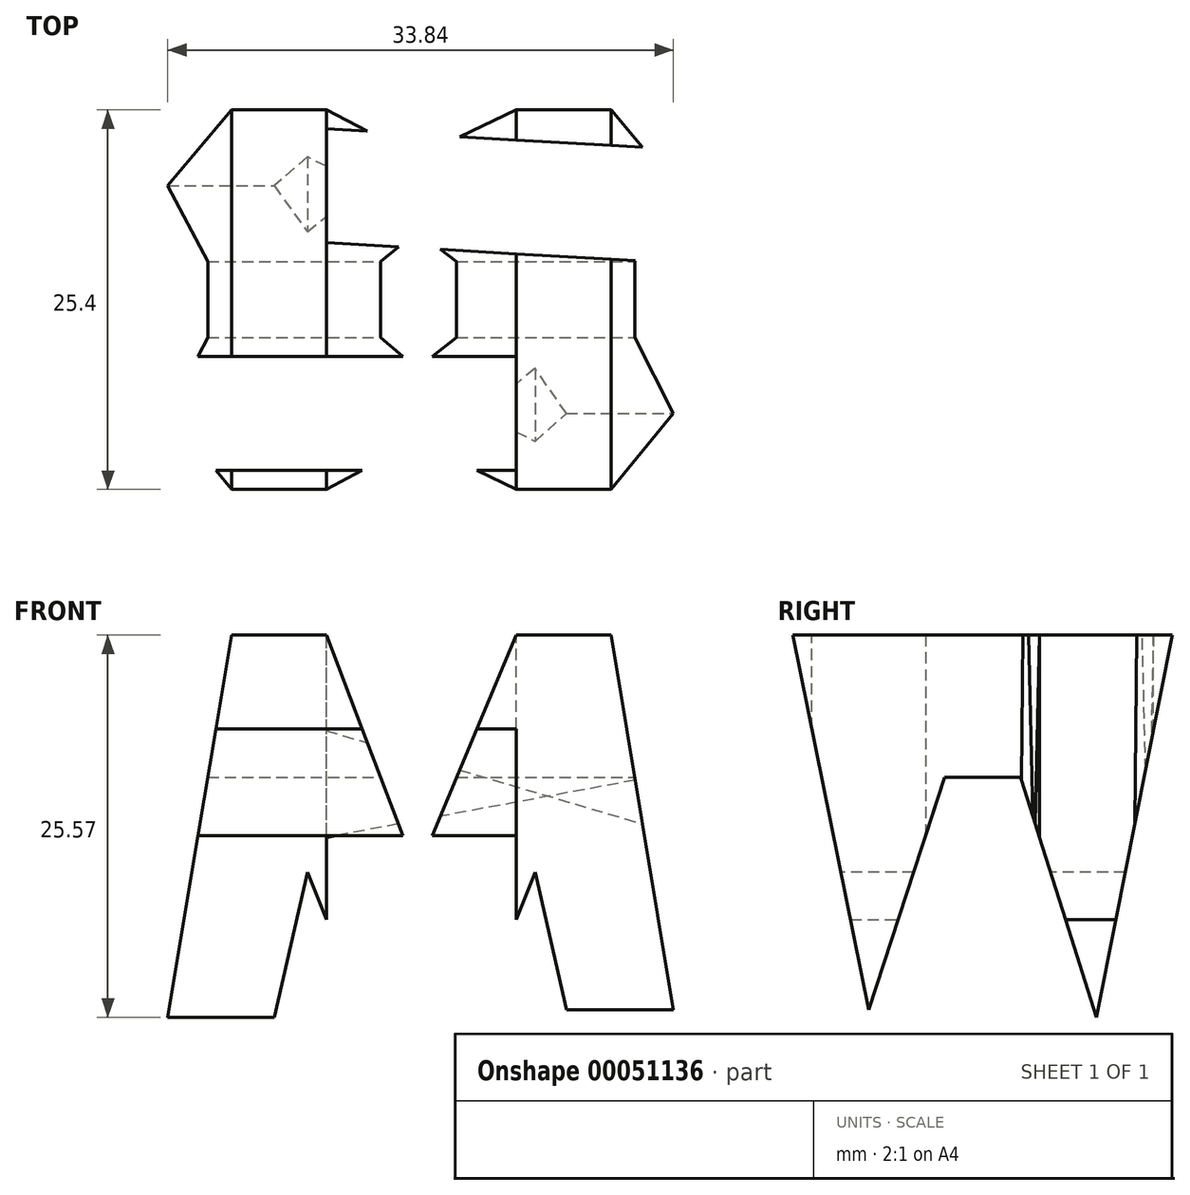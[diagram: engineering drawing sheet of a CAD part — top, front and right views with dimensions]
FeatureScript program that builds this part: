
annotation { "Feature Type Name" : "Feature", "Feature Type Description" : "" }
export const myFeature = defineFeature(function(context is Context, id is Id, definition is map)
    precondition{}
    {
        {
            var Q0;
            Q0=qCreatedBy(makeId("Front.planeOp"),FACE);
            var sketch = newSketch(context, id + "F0", { "sketchPlane" : qUnion([Q0])});
            skLineSegment(sketch, "E0.bottom", {"start": v(0, 0) * mm, "end": v(38.1, 0) * mm});
            skLineSegment(sketch, "E0.top", {"start": v(0, 38.1) * mm, "end": v(38.1, 38.1) * mm});
            skLineSegment(sketch, "E0.left", {"start": v(0, 0) * mm, "end": v(0, 38.1) * mm});
            skLineSegment(sketch, "E0.right", {"start": v(38.1, 0) * mm, "end": v(38.1, 38.1) * mm});
            skSolve(sketch);
        }
        {
            var Q0;
            Q0=makeQuery(id+"F0.imprint","IMPRINT",FACE,{"disambiguationData":[TD([[makeQuery(id+"F0.imprint","IMPRINT",EDGE,{"derivedFrom":sQuery(id+"F0.wireOp",EDGE,"E0.bottom")}),1.0]])]});
            extrude(context, id + "F1", {"entities" : qUnion([Q0]), "depth" : 38.1 * mm});
        }
        {
            var Q0;
            Q0=makeQuery(id+"F1.opExtrude","CAP_FACE",FACE,{"disambiguationData":[OSD([sQuery(id+"F0.wireOp",EDGE,"E0.bottom"),sQuery(id+"F0.wireOp",EDGE,"E0.top"),sQuery(id+"F0.wireOp",EDGE,"E0.left"),sQuery(id+"F0.wireOp",EDGE,"E0.right")])],"isStart":false});
            cPlane(context, id + "F2", {"entities" : qUnion([Q0]), "cplaneType" : CPlaneType.OFFSET, "offset" : 38.1 * mm, "width" : 152.4 * mm, "height" : 152.4 * mm});
        }
        {
            var Q0;
            Q0=makeQuery(id+"F1.opExtrude","SWEPT_FACE",FACE,{"disambiguationData":[OSD([sQuery(id+"F0.wireOp",EDGE,"E0.right")])]});
            cPlane(context, id + "F3", {"entities" : qUnion([Q0]), "cplaneType" : CPlaneType.OFFSET, "offset" : 38.1 * mm, "width" : 152.4 * mm, "height" : 152.4 * mm});
        }
        {
            var Q0;
            Q0=makeQuery(id+"F1.opExtrude","SWEPT_FACE",FACE,{"disambiguationData":[OSD([sQuery(id+"F0.wireOp",EDGE,"E0.top")])]});
            cPlane(context, id + "F4", {"entities" : qUnion([Q0]), "cplaneType" : CPlaneType.OFFSET, "offset" : 38.1 * mm, "width" : 152.4 * mm, "height" : 152.4 * mm});
        }
        {
            var Q0;
            Q0=qCreatedBy(id+"F3.planeOp",FACE);
            var sketch = newSketch(context, id + "F5", { "sketchPlane" : qUnion([Q0])});
            skLineSegment(sketch, "E1", {"start": v(0, 0) * mm, "end": v(-38.1, 0) * mm});
            skLineSegment(sketch, "E2", {"start": v(-38.1, 0) * mm, "end": v(-38.1, 38.1) * mm});
            skLineSegment(sketch, "E3", {"start": v(-38.1, 38.1) * mm, "end": v(0, 38.1) * mm});
            skLineSegment(sketch, "E4", {"start": v(0, 38.1) * mm, "end": v(0, 0) * mm});
            skLineSegment(sketch, "E5", {"start": v(-38.1, 38.1) * mm, "end": v(-31.75, 0) * mm});
            skLineSegment(sketch, "E6", {"start": v(-31.75, 38.1) * mm, "end": v(-26.67, 13.01) * mm});
            skLineSegment(sketch, "E7", {"start": v(-26.67, 13.01) * mm, "end": v(-21.59, 28.58) * mm});
            skLineSegment(sketch, "E8", {"start": v(-21.59, 28.58) * mm, "end": v(-16.5, 28.58) * mm});
            skLineSegment(sketch, "E9", {"start": v(-16.5, 28.58) * mm, "end": v(-11.43, 12.53) * mm});
            skLineSegment(sketch, "E10", {"start": v(-11.43, 12.53) * mm, "end": v(-6.35, 38.1) * mm});
            skLineSegment(sketch, "E11", {"start": v(0, 38.1) * mm, "end": v(-6.35, 0) * mm});
            skLineSegment(sketch, "E12", {"start": v(-25.4, 0) * mm, "end": v(-19.05, 15.88) * mm});
            skLineSegment(sketch, "E13", {"start": v(-19.05, 15.88) * mm, "end": v(-12.7, 0) * mm});
            skLineSegment(sketch, "E14", {"start": v(-38.1, 38.1) * mm, "end": v(-31.75, 38.1) * mm});
            skLineSegment(sketch, "E15", {"start": v(-6.35, 38.1) * mm, "end": v(0, 38.1) * mm});
            skPoint(sketch, "E16", {"position": v(-19.05, 0) * mm});
            skSolve(sketch);
        }
        {
            var Q0;
            Q0=makeQuery(id+"F5.imprint","IMPRINT",FACE,{"disambiguationData":[TD([[makeQuery(id+"F5.imprint","IMPRINT",EDGE,{"derivedFrom":sQuery(id+"F5.wireOp",EDGE,"E3")}),-1.0]])]});
            var Q1;
            {var subQ0=sQuery(id+"F5.wireOp",EDGE,"E12");Q1=makeQuery(id+"F5.imprint","IMPRINT",FACE,{"disambiguationData":[TD([[makeQuery(id+"F5.imprint","IMPRINT",EDGE,{"derivedFrom":subQ0}),-1.0]])]});}
            var Q2;
            {var subQ0=sQuery(id+"F5.wireOp",EDGE,"E2");Q2=makeQuery(id+"F5.imprint","IMPRINT",FACE,{"disambiguationData":[TD([[makeQuery(id+"F5.imprint","IMPRINT",EDGE,{"derivedFrom":subQ0}),-1.0]])]});}
            var Q3;
            {var subQ0=sQuery(id+"F5.wireOp",EDGE,"E4");Q3=makeQuery(id+"F5.imprint","IMPRINT",FACE,{"disambiguationData":[TD([[makeQuery(id+"F5.imprint","IMPRINT",EDGE,{"derivedFrom":subQ0}),-1.0]])]});}
            extrude(context, id + "F6", {"entities" : qUnion([Q0, Q1, Q2, Q3]), "operationType" : NewBodyOperationType.REMOVE, "oppositeDirection" : true, "depth" : 76.2 * mm});
        }
        {
            var Q0;
            Q0=qCreatedBy(id+"F2.planeOp",FACE);
            var sketch = newSketch(context, id + "F7", { "sketchPlane" : qUnion([Q0])});
            skLineSegment(sketch, "E17", {"start": v(0, 38.1) * mm, "end": v(38.1, 38.1) * mm});
            skLineSegment(sketch, "E18", {"start": v(38.1, 38.1) * mm, "end": v(38.1, 0) * mm});
            skLineSegment(sketch, "E19", {"start": v(31.75, 0) * mm, "end": v(0, 0) * mm});
            skLineSegment(sketch, "E20", {"start": v(0, 0) * mm, "end": v(0, 38.1) * mm});
            skLineSegment(sketch, "E21", {"start": v(0, 0) * mm, "end": v(6.35, 38.1) * mm});
            skLineSegment(sketch, "E22", {"start": v(12.7, 38.1) * mm, "end": v(18.76, 22.23) * mm});
            skLineSegment(sketch, "E23", {"start": v(18.76, 22.23) * mm, "end": v(25.4, 38.1) * mm});
            skLineSegment(sketch, "E24", {"start": v(31.75, 38.1) * mm, "end": v(38.1, 0) * mm});
            skLineSegment(sketch, "E25", {"start": v(6.35, 0) * mm, "end": v(11.43, 22.23) * mm});
            skLineSegment(sketch, "E26", {"start": v(11.43, 22.23) * mm, "end": v(16.51, 9.53) * mm});
            skLineSegment(sketch, "E27", {"start": v(16.5, 9.53) * mm, "end": v(21.59, 9.53) * mm});
            skLineSegment(sketch, "E28", {"start": v(21.59, 9.53) * mm, "end": v(26.67, 22.22) * mm});
            skLineSegment(sketch, "E29", {"start": v(26.67, 22.22) * mm, "end": v(31.75, 0) * mm});
            skPoint(sketch, "E30", {"position": v(19.05, 38.1) * mm});
            skSolve(sketch);
        }
        {
            var Q0;
            {var subQ0=sQuery(id+"F7.wireOp",EDGE,"E22");Q0=makeQuery(id+"F7.imprint","IMPRINT",FACE,{"disambiguationData":[TD([[makeQuery(id+"F7.imprint","IMPRINT",EDGE,{"derivedFrom":subQ0}),1.0]])]});}
            var Q1;
            {var subQ0=sQuery(id+"F7.wireOp",EDGE,"E20");Q1=makeQuery(id+"F7.imprint","IMPRINT",FACE,{"disambiguationData":[TD([[makeQuery(id+"F7.imprint","IMPRINT",EDGE,{"derivedFrom":subQ0}),-1.0]])]});}
            var Q2;
            {var subQ0=sQuery(id+"F7.wireOp",EDGE,"E25");Q2=makeQuery(id+"F7.imprint","IMPRINT",FACE,{"disambiguationData":[TD([[makeQuery(id+"F7.imprint","IMPRINT",EDGE,{"derivedFrom":subQ0}),-1.0]])]});}
            var Q3;
            {var subQ0=sQuery(id+"F7.wireOp",EDGE,"E18");Q3=makeQuery(id+"F7.imprint","IMPRINT",FACE,{"disambiguationData":[TD([[makeQuery(id+"F7.imprint","IMPRINT",EDGE,{"derivedFrom":subQ0}),-1.0]])]});}
            extrude(context, id + "F8", {"entities" : qUnion([Q0, Q1, Q2, Q3]), "operationType" : NewBodyOperationType.REMOVE, "oppositeDirection" : true, "depth" : 76.2 * mm});
        }
        {
            var Q0;
            Q0=qCreatedBy(id+"F4.planeOp",FACE);
            var sketch = newSketch(context, id + "F9", { "sketchPlane" : qUnion([Q0])});
            skLineSegment(sketch, "E31", {"start": v(0, 0) * mm, "end": v(38.1, 0) * mm});
            skLineSegment(sketch, "E32", {"start": v(38.1, 0) * mm, "end": v(38.1, -38.1) * mm});
            skLineSegment(sketch, "E33", {"start": v(38.1, -38.1) * mm, "end": v(0, -38.1) * mm});
            skLineSegment(sketch, "E34", {"start": v(0, -38.1) * mm, "end": v(0, 0) * mm});
            skLineSegment(sketch, "E35", {"start": v(38.1, -9.1) * mm, "end": v(12.7, -7.62) * mm});
            skLineSegment(sketch, "E36", {"start": v(12.7, -7.62) * mm, "end": v(12.7, -15.24) * mm});
            skLineSegment(sketch, "E37", {"start": v(12.7, -15.24) * mm, "end": v(38.1, -16.73) * mm});
            skLineSegment(sketch, "E38", {"start": v(0, -22.86) * mm, "end": v(25.4, -22.86) * mm});
            skLineSegment(sketch, "E39", {"start": v(25.4, -22.86) * mm, "end": v(25.4, -30.48) * mm});
            skLineSegment(sketch, "E40", {"start": v(25.4, -30.48) * mm, "end": v(0, -30.48) * mm});
            skSolve(sketch);
        }
        {
            var Q0;
            {var subQ0=sQuery(id+"F9.wireOp",EDGE,"E35");Q0=makeQuery(id+"F9.imprint","IMPRINT",FACE,{"disambiguationData":[TD([[makeQuery(id+"F9.imprint","IMPRINT",EDGE,{"derivedFrom":subQ0}),1.0]])]});}
            var Q1;
            {var subQ0=sQuery(id+"F9.wireOp",EDGE,"E38");Q1=makeQuery(id+"F9.imprint","IMPRINT",FACE,{"disambiguationData":[TD([[makeQuery(id+"F9.imprint","IMPRINT",EDGE,{"derivedFrom":subQ0}),-1.0]])]});}
            extrude(context, id + "F10", {"entities" : qUnion([Q0, Q1]), "operationType" : NewBodyOperationType.REMOVE, "oppositeDirection" : true, "depth" : 76.2 * mm});
        }
    });
